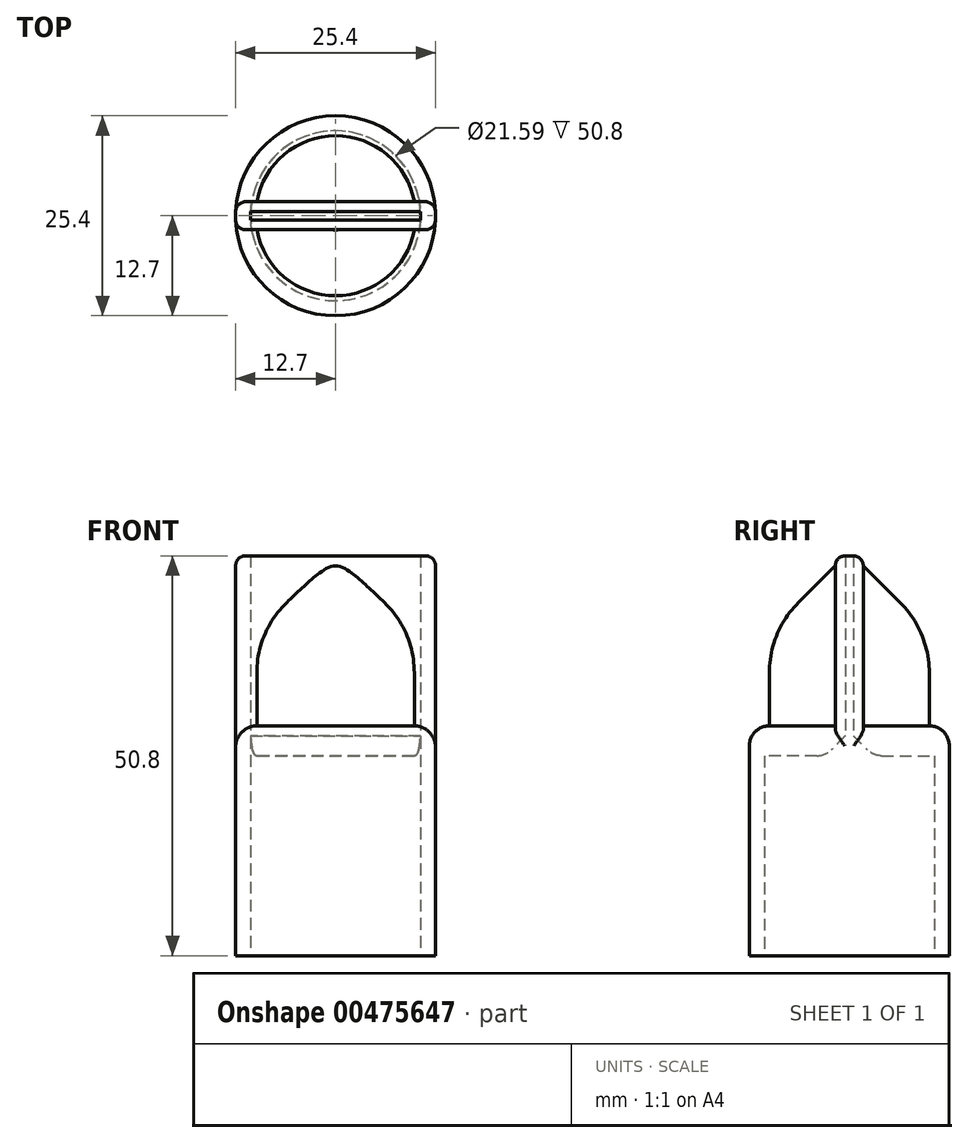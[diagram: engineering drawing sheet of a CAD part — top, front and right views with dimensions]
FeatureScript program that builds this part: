
annotation { "Feature Type Name" : "Feature", "Feature Type Description" : "" }
export const myFeature = defineFeature(function(context is Context, id is Id, definition is map)
    precondition{}
    {
        {
            var Q0;
            Q0=qCreatedBy(makeId("Top.planeOp"),FACE);
            var sketch = newSketch(context, id + "F0", { "sketchPlane" : qUnion([Q0])});
            skCircle(sketch, "E0", {"center": v(0, 0) * mm, "radius": 10.8 * mm});
            skCircle(sketch, "E1", {"center": v(0, 0) * mm, "radius": 12.7 * mm});
            skSolve(sketch);
        }
        {
            var Q0;
            Q0=makeQuery(id+"F0.imprint","IMPRINT",FACE,{"disambiguationData":[TD([[makeQuery(id+"F0.imprint","IMPRINT",EDGE,{"derivedFrom":sQuery(id+"F0.wireOp",EDGE,"E0")}),-1.0]])]});
            extrude(context, id + "F1", {"entities" : qUnion([Q0]), "depth" : 25.4 * mm});
        }
        {
            var Q0;
            Q0=makeQuery(id+"F1.opExtrude","CAP_FACE",FACE,{"disambiguationData":[OSD([sQuery(id+"F0.wireOp",EDGE,"E0"),sQuery(id+"F0.wireOp",EDGE,"E1")])],"isStart":false});
            var sketch = newSketch(context, id + "F2", { "sketchPlane" : qUnion([Q0])});
            skLineSegment(sketch, "E2", {"start": v(0, 0) * mm, "end": v(12.7, 0) * mm});
            skLineSegment(sketch, "E3", {"start": v(0, 0) * mm, "end": v(-12.7, 0) * mm});
            skLineSegment(sketch, "E4", {"start": v(0, 0) * mm, "end": v(0, -0.52) * mm});
            skLineSegment(sketch, "E5", {"start": v(0, -0.52) * mm, "end": v(12.69, -0.52) * mm});
            skLineSegment(sketch, "E6", {"start": v(0, -0.52) * mm, "end": v(-12.69, -0.52) * mm});
            skLineSegment(sketch, "E7", {"start": v(0, 0) * mm, "end": v(0, 0.5) * mm});
            skLineSegment(sketch, "E8", {"start": v(0, 0.5) * mm, "end": v(-12.7, 0.5) * mm});
            skLineSegment(sketch, "E9", {"start": v(0, 0.5) * mm, "end": v(12.69, 0.5) * mm});
            skPoint(sketch, "E9.endSnap0", {"position": v(12.69, 0.38) * mm});
            skLineSegment(sketch, "E10", {"start": v(-12.58, 1.77) * mm, "end": v(12.58, 1.77) * mm});
            skLineSegment(sketch, "E11", {"start": v(-12.57, -1.78) * mm, "end": v(12.57, -1.78) * mm});
            skSolve(sketch);
        }
        {
            var Q0;
            {var subQ0=sQuery(id+"F2.wireOp",EDGE,"E8");var subQ1=makeQuery(id+"F1.opExtrude","CAP_EDGE",EDGE,{"disambiguationData":[OSD([sQuery(id+"F0.wireOp",EDGE,"E1")])],"isStart":false});var subQ2=makeQuery(id+"F2.imprint","INTERSECT",VERTEX,{"derivedFrom":[subQ1,subQ0]});Q0=makeQuery(id+"F2.imprint","IMPRINT",FACE,{"disambiguationData":[TD([[makeQuery(id+"F2.imprint","IMPRINT",EDGE,{"disambiguationData":[TD([[subQ2,1.0]])],"derivedFrom":subQ0}),-1.0]])]});}
            var Q1;
            {var subQ0=sQuery(id+"F2.wireOp",EDGE,"E3");var subQ1=makeQuery(id+"F1.opExtrude","CAP_EDGE",EDGE,{"disambiguationData":[OSD([sQuery(id+"F0.wireOp",EDGE,"E1")])],"isStart":false});var subQ2=makeQuery(id+"F2.imprint","INTERSECT",VERTEX,{"derivedFrom":[subQ1,subQ0]});Q1=makeQuery(id+"F2.imprint","IMPRINT",FACE,{"disambiguationData":[TD([[makeQuery(id+"F2.imprint","IMPRINT",EDGE,{"disambiguationData":[TD([[subQ2,1.0]])],"derivedFrom":subQ0}),-1.0]])]});}
            var Q2;
            {var subQ0=sQuery(id+"F2.wireOp",EDGE,"E3");var subQ1=makeQuery(id+"F1.opExtrude","CAP_EDGE",EDGE,{"disambiguationData":[OSD([sQuery(id+"F0.wireOp",EDGE,"E1")])],"isStart":false});var subQ2=makeQuery(id+"F2.imprint","INTERSECT",VERTEX,{"derivedFrom":[subQ1,subQ0]});Q2=makeQuery(id+"F2.imprint","IMPRINT",FACE,{"disambiguationData":[TD([[makeQuery(id+"F2.imprint","IMPRINT",EDGE,{"disambiguationData":[TD([[subQ2,1.0]])],"derivedFrom":subQ0}),1.0]])]});}
            var Q3;
            {var subQ0=sQuery(id+"F2.wireOp",EDGE,"E6");var subQ1=makeQuery(id+"F1.opExtrude","CAP_EDGE",EDGE,{"disambiguationData":[OSD([sQuery(id+"F0.wireOp",EDGE,"E1")])],"isStart":false});var subQ2=makeQuery(id+"F2.imprint","INTERSECT",VERTEX,{"derivedFrom":[subQ1,subQ0]});Q3=makeQuery(id+"F2.imprint","IMPRINT",FACE,{"disambiguationData":[TD([[makeQuery(id+"F2.imprint","IMPRINT",EDGE,{"disambiguationData":[TD([[subQ2,1.0]])],"derivedFrom":subQ0}),1.0]])]});}
            var Q4;
            {var subQ2=sQuery(id+"F2.wireOp",EDGE,"E2");var subQ4=makeQuery(id+"F1.opExtrude","CAP_EDGE",EDGE,{"disambiguationData":[OSD([sQuery(id+"F0.wireOp",EDGE,"E1")])],"isStart":false});var subQ5=makeQuery(id+"F2.imprint","INTERSECT",VERTEX,{"derivedFrom":[subQ4,subQ2]});Q4=makeQuery(id+"F2.imprint","IMPRINT",FACE,{"disambiguationData":[TD([[makeQuery(id+"F2.imprint","IMPRINT",EDGE,{"disambiguationData":[TD([[subQ5,1.0]])],"derivedFrom":subQ2}),1.0]])]});}
            var Q5;
            {var subQ0=sQuery(id+"F2.wireOp",EDGE,"E5");var subQ1=makeQuery(id+"F1.opExtrude","CAP_EDGE",EDGE,{"disambiguationData":[OSD([sQuery(id+"F0.wireOp",EDGE,"E1")])],"isStart":false});var subQ2=makeQuery(id+"F2.imprint","INTERSECT",VERTEX,{"derivedFrom":[subQ1,subQ0]});Q5=makeQuery(id+"F2.imprint","IMPRINT",FACE,{"disambiguationData":[TD([[makeQuery(id+"F2.imprint","IMPRINT",EDGE,{"disambiguationData":[TD([[subQ2,1.0]])],"derivedFrom":subQ0}),-1.0]])]});}
            var Q6;
            {var subQ0=sQuery(id+"F2.wireOp",EDGE,"E2");var subQ1=makeQuery(id+"F1.opExtrude","CAP_EDGE",EDGE,{"disambiguationData":[OSD([sQuery(id+"F0.wireOp",EDGE,"E1")])],"isStart":false});var subQ2=makeQuery(id+"F2.imprint","INTERSECT",VERTEX,{"derivedFrom":[subQ1,subQ0]});Q6=makeQuery(id+"F2.imprint","IMPRINT",FACE,{"disambiguationData":[TD([[makeQuery(id+"F2.imprint","IMPRINT",EDGE,{"disambiguationData":[TD([[subQ2,1.0]])],"derivedFrom":subQ0}),-1.0]])]});}
            var Q7;
            {var subQ1=makeQuery(id+"F1.opExtrude","CAP_EDGE",EDGE,{"disambiguationData":[OSD([sQuery(id+"F0.wireOp",EDGE,"E0")])],"isStart":false});var subQ3=sQuery(id+"F2.wireOp",EDGE,"E10");var subQ5=makeQuery(id+"F2.imprint","INTERSECT",VERTEX,{"disambiguationData":[OD(0.0)],"derivedFrom":[subQ1,subQ3]});Q7=makeQuery(id+"F2.imprint","IMPRINT",FACE,{"disambiguationData":[TD([[makeQuery(id+"F2.imprint","IMPRINT",EDGE,{"disambiguationData":[TD([[subQ5,-1.0]])],"derivedFrom":subQ3}),-1.0]])]});}
            var Q8;
            {var subQ1=makeQuery(id+"F1.opExtrude","CAP_EDGE",EDGE,{"disambiguationData":[OSD([sQuery(id+"F0.wireOp",EDGE,"E0")])],"isStart":false});var subQ3=sQuery(id+"F2.wireOp",EDGE,"E11");var subQ5=makeQuery(id+"F2.imprint","INTERSECT",VERTEX,{"disambiguationData":[OD(0.0)],"derivedFrom":[subQ1,subQ3]});Q8=makeQuery(id+"F2.imprint","IMPRINT",FACE,{"disambiguationData":[TD([[makeQuery(id+"F2.imprint","IMPRINT",EDGE,{"disambiguationData":[TD([[subQ5,-1.0]])],"derivedFrom":subQ3}),1.0]])]});}
            extrude(context, id + "F3", {"entities" : qUnion([Q0, Q1, Q2, Q3, Q4, Q5, Q6, Q7, Q8]), "operationType" : NewBodyOperationType.ADD, "depth" : 25.4 * mm});
        }
        {
            var Q0;
            Q0=makeQuery(id+"F3.opExtrude","SWEPT_FACE",FACE,{"disambiguationData":[OSD([sQuery(id+"F2.wireOp",EDGE,"E10")])]});
            var sketch = newSketch(context, id + "F4", { "sketchPlane" : qUnion([Q0])});
            skLineSegment(sketch, "E12.bottom", {"start": v(-12.58, 25.4) * mm, "end": v(12.58, 25.4) * mm});
            skLineSegment(sketch, "E12.top", {"start": v(-12.58, 29.21) * mm, "end": v(12.58, 29.21) * mm});
            skLineSegment(sketch, "E12.left", {"start": v(-12.58, 25.4) * mm, "end": v(-12.58, 29.21) * mm});
            skLineSegment(sketch, "E12.right", {"start": v(12.58, 25.4) * mm, "end": v(12.58, 29.21) * mm});
            skSolve(sketch);
        }
        {
            var Q0;
            Q0=makeQuery(id+"F4.imprint","IMPRINT",FACE,{"disambiguationData":[TD([[makeQuery(id+"F4.imprint","IMPRINT",EDGE,{"derivedFrom":sQuery(id+"F4.wireOp",EDGE,"E12.top")}),-1.0]])]});
            extrude(context, id + "F5", {"entities" : qUnion([Q0]), "operationType" : NewBodyOperationType.ADD, "depth" : 25.4 * mm});
        }
        {
            var Q0;
            Q0=makeQuery(id+"F3.opExtrude","SWEPT_FACE",FACE,{"disambiguationData":[OSD([sQuery(id+"F2.wireOp",EDGE,"E11")])]});
            var sketch = newSketch(context, id + "F6", { "sketchPlane" : qUnion([Q0])});
            skLineSegment(sketch, "E13.bottom", {"start": v(-12.57, 25.4) * mm, "end": v(12.57, 25.4) * mm});
            skLineSegment(sketch, "E13.top", {"start": v(-12.57, 29.21) * mm, "end": v(12.57, 29.21) * mm});
            skLineSegment(sketch, "E13.left", {"start": v(-12.57, 25.4) * mm, "end": v(-12.57, 29.21) * mm});
            skLineSegment(sketch, "E13.right", {"start": v(12.57, 25.4) * mm, "end": v(12.57, 29.21) * mm});
            skSolve(sketch);
        }
        {
            var Q0;
            Q0=makeQuery(id+"F6.imprint","IMPRINT",FACE,{"disambiguationData":[TD([[makeQuery(id+"F6.imprint","IMPRINT",EDGE,{"derivedFrom":sQuery(id+"F6.wireOp",EDGE,"E13.top")}),-1.0]])]});
            extrude(context, id + "F7", {"entities" : qUnion([Q0]), "operationType" : NewBodyOperationType.ADD, "depth" : 25.4 * mm});
        }
        {
            var Q0;
            Q0=makeQuery(id+"F7.boolean.opBoolean","SPLIT",FACE,{"derivedFrom":makeQuery(id+"F7.opExtrude","SWEPT_FACE",FACE,{"disambiguationData":[OSD([sQuery(id+"F6.wireOp",EDGE,"E13.bottom")])]})});
            var Q1;
            Q1=makeQuery(id+"F5.boolean.opBoolean","SPLIT",FACE,{"derivedFrom":makeQuery(id+"F5.opExtrude","SWEPT_FACE",FACE,{"disambiguationData":[OSD([sQuery(id+"F4.wireOp",EDGE,"E12.bottom")])]})});
            extrude(context, id + "F8", {"entities" : qUnion([Q0, Q1]), "operationType" : NewBodyOperationType.REMOVE, "oppositeDirection" : true, "depth" : 25.4 * mm});
        }
        {
            var Q0;
            {var subQ0=sQuery(id+"F2.wireOp",EDGE,"E11");var subQ1=sQuery(id+"F0.wireOp",EDGE,"E1");Q0=makeQuery(id+"F7.boolean.opBoolean","SPLIT",EDGE,{"derivedFrom":makeQuery(id+"F3.opExtrude","SWEPT_EDGE",EDGE,{"disambiguationData":[OSD([subQ1,subQ0]),TDD([makeQuery(id+"F2.imprint","INTERSECT",VERTEX,{"disambiguationData":[OD(0.0)],"derivedFrom":[makeQuery(id+"F1.opExtrude","CAP_EDGE",EDGE,{"disambiguationData":[OSD([subQ1])],"isStart":false}),subQ0]})])]})});}
            var Q1;
            {var subQ0=sQuery(id+"F2.wireOp",EDGE,"E11");var subQ1=sQuery(id+"F0.wireOp",EDGE,"E1");Q1=makeQuery(id+"F7.boolean.opBoolean","SPLIT",EDGE,{"derivedFrom":makeQuery(id+"F3.opExtrude","SWEPT_EDGE",EDGE,{"disambiguationData":[OSD([subQ1,subQ0]),TDD([makeQuery(id+"F2.imprint","INTERSECT",VERTEX,{"disambiguationData":[OD(1.0)],"derivedFrom":[makeQuery(id+"F1.opExtrude","CAP_EDGE",EDGE,{"disambiguationData":[OSD([subQ1])],"isStart":false}),subQ0]})])]})});}
            var Q2;
            {var subQ0=sQuery(id+"F2.wireOp",EDGE,"E10");var subQ1=sQuery(id+"F0.wireOp",EDGE,"E1");Q2=makeQuery(id+"F5.boolean.opBoolean","SPLIT",EDGE,{"derivedFrom":makeQuery(id+"F3.opExtrude","SWEPT_EDGE",EDGE,{"disambiguationData":[OSD([subQ1,subQ0]),TDD([makeQuery(id+"F2.imprint","INTERSECT",VERTEX,{"disambiguationData":[OD(1.0)],"derivedFrom":[makeQuery(id+"F1.opExtrude","CAP_EDGE",EDGE,{"disambiguationData":[OSD([subQ1])],"isStart":false}),subQ0]})])]})});}
            var Q3;
            {var subQ0=sQuery(id+"F2.wireOp",EDGE,"E10");var subQ1=sQuery(id+"F0.wireOp",EDGE,"E1");Q3=makeQuery(id+"F5.boolean.opBoolean","SPLIT",EDGE,{"derivedFrom":makeQuery(id+"F3.opExtrude","SWEPT_EDGE",EDGE,{"disambiguationData":[OSD([subQ1,subQ0]),TDD([makeQuery(id+"F2.imprint","INTERSECT",VERTEX,{"disambiguationData":[OD(0.0)],"derivedFrom":[makeQuery(id+"F1.opExtrude","CAP_EDGE",EDGE,{"disambiguationData":[OSD([subQ1])],"isStart":false}),subQ0]})])]})});}
            fillet(context, id + "F9", {"entities" : qUnion([Q0, Q1, Q2, Q3]), "radius" : 1.27 * mm, "tangentPropagation" : true, "allowEdgeOverflow" : false});
        }
        {
            var Q0;
            {var subQ0=sQuery(id+"F0.wireOp",EDGE,"E1");var subQ1=makeQuery(id+"F1.opExtrude","CAP_EDGE",EDGE,{"disambiguationData":[OSD([subQ0])],"isStart":false});var subQ3=sQuery(id+"F2.wireOp",EDGE,"E11");Q0=makeQuery(id+"F8.boolean.opBoolean","INTERSECT",EDGE,{"derivedFrom":[makeQuery(id+"F7.opExtrude","SWEPT_FACE",FACE,{"disambiguationData":[OSD([sQuery(id+"F6.wireOp",EDGE,"E13.top")])]}),makeQuery(id+"F8.opExtrude","SWEPT_FACE",FACE,{"disambiguationData":[OSD([subQ0]),TDD([makeQuery(id+"F3.boolean.opBoolean","SPLIT",EDGE,{"disambiguationData":[TD([makeQuery(id+"F3.opExtrude","SWEPT_FACE",FACE,{"disambiguationData":[OSD([subQ3])]})])],"derivedFrom":subQ1})])]})]});}
            var Q1;
            {var subQ0=sQuery(id+"F0.wireOp",EDGE,"E1");var subQ1=makeQuery(id+"F1.opExtrude","CAP_EDGE",EDGE,{"disambiguationData":[OSD([subQ0])],"isStart":false});var subQ5=sQuery(id+"F2.wireOp",EDGE,"E10");Q1=makeQuery(id+"F8.boolean.opBoolean","INTERSECT",EDGE,{"derivedFrom":[makeQuery(id+"F5.opExtrude","SWEPT_FACE",FACE,{"disambiguationData":[OSD([sQuery(id+"F4.wireOp",EDGE,"E12.top")])]}),makeQuery(id+"F8.opExtrude","SWEPT_FACE",FACE,{"disambiguationData":[OSD([subQ0]),TDD([makeQuery(id+"F3.boolean.opBoolean","SPLIT",EDGE,{"disambiguationData":[TD([makeQuery(id+"F3.opExtrude","SWEPT_FACE",FACE,{"disambiguationData":[OSD([subQ5])]})])],"derivedFrom":subQ1})])]})]});}
            fillet(context, id + "F10", {"entities" : qUnion([Q0, Q1]), "radius" : 2.54 * mm, "tangentPropagation" : true, "allowEdgeOverflow" : false});
        }
        {
            var Q0;
            Q0=makeQuery(id+"F3.opExtrude","CAP_EDGE",EDGE,{"disambiguationData":[OSD([sQuery(id+"F2.wireOp",EDGE,"E5"),sQuery(id+"F2.wireOp",EDGE,"E6")])],"isStart":true});
            var Q1;
            Q1=makeQuery(id+"F3.opExtrude","CAP_EDGE",EDGE,{"disambiguationData":[OSD([sQuery(id+"F2.wireOp",EDGE,"E8"),sQuery(id+"F2.wireOp",EDGE,"E9")])],"isStart":true});
            chamfer(context, id + "F11", {"entities" : qUnion([Q0, Q1]), "width" : 2.54 * mm, "tangentPropagation" : true});
        }
        {
            var Q0;
            {var subQ0=sQuery(id+"FHGbkbRZZd5fJVd_1.wireOp",EDGE,"k0sFFGCa-SWWJ-xCFf-tX0p-m5kxG7faOtJC");Q0=makeQuery(id+"FhUnpWBAYJd5fCt_1.opExtrude","CAP_EDGE",EDGE,{"disambiguationData":[OSD([subQ0]),TDD([makeQuery(id+"FHGbkbRZZd5fJVd_1.imprint","IMPRINT",EDGE,{"disambiguationData":[TD([[makeQuery(id+"FHGbkbRZZd5fJVd_1.imprint","INTERSECT",VERTEX,{"disambiguationData":[OD(1.0)],"derivedFrom":[makeQuery(id+"F3.opExtrude","CAP_EDGE",EDGE,{"disambiguationData":[OSD([sQuery(id+"F2.wireOp",EDGE,"E8"),sQuery(id+"F2.wireOp",EDGE,"E9")])],"isStart":false}),subQ0]}),-1.0]])],"derivedFrom":subQ0})])],"isStart":false});}
            var Q1;
            {var subQ0=sQuery(id+"FHGbkbRZZd5fJVd_1.wireOp",EDGE,"k0sFFGCa-SWWJ-xCFf-tX0p-m5kxG7faOtJC");Q1=makeQuery(id+"FhUnpWBAYJd5fCt_1.opExtrude","CAP_EDGE",EDGE,{"disambiguationData":[OSD([subQ0]),TDD([makeQuery(id+"FHGbkbRZZd5fJVd_1.imprint","IMPRINT",EDGE,{"disambiguationData":[TD([[makeQuery(id+"FHGbkbRZZd5fJVd_1.imprint","INTERSECT",VERTEX,{"disambiguationData":[OD(0.0)],"derivedFrom":[makeQuery(id+"F3.opExtrude","CAP_EDGE",EDGE,{"disambiguationData":[OSD([sQuery(id+"F2.wireOp",EDGE,"E8"),sQuery(id+"F2.wireOp",EDGE,"E9")])],"isStart":false}),subQ0]}),1.0]])],"derivedFrom":subQ0})])],"isStart":false});}
            var Q2;
            {var subQ0=sQuery(id+"F2.wireOp",EDGE,"E9");var subQ1=sQuery(id+"F2.wireOp",EDGE,"E8");var subQ2=sQuery(id+"F2.wireOp",EDGE,"E10");var subQ3=sQuery(id+"F0.wireOp",EDGE,"E1");var subQ4=sQuery(id+"F0.wireOp",EDGE,"E0");var subQ7=sQuery(id+"F2.wireOp",EDGE,"E5");var subQ9=sQuery(id+"F2.wireOp",EDGE,"E6");Q2=makeQuery(id+"F11.opChamfer","BLEND_EDGE",EDGE,{"blendedFrom":[makeQuery(id+"F3.opExtrude","CAP_EDGE",EDGE,{"disambiguationData":[OSD([subQ1,subQ0])],"isStart":true}),makeQuery(id+"F5.boolean.opBoolean","MERGE",FACE,{"derivedFrom":[makeQuery(id+"F3.boolean.opBoolean","SPLIT",FACE,{"disambiguationData":[TD([makeQuery(id+"F3.opExtrude","SWEPT_FACE",FACE,{"disambiguationData":[OSD([subQ2])]})])],"derivedFrom":makeQuery(id+"F3.opExtrude","CAP_FACE",FACE,{"disambiguationData":[OSD([subQ4,subQ3,subQ7,subQ9,subQ1,subQ0,subQ2,sQuery(id+"F2.wireOp",EDGE,"E11")])],"isStart":true})}),makeQuery(id+"F5.opExtrude","SWEPT_FACE",FACE,{"disambiguationData":[OSD([sQuery(id+"F4.wireOp",EDGE,"E12.bottom")])]})]})],"blendedInto":[makeQuery(id+"F5.boolean.opBoolean","MERGE",FACE,{"derivedFrom":[makeQuery(id+"F3.boolean.opBoolean","SPLIT",FACE,{"disambiguationData":[TD([makeQuery(id+"F3.opExtrude","SWEPT_FACE",FACE,{"disambiguationData":[OSD([subQ2])]})])],"derivedFrom":makeQuery(id+"F3.opExtrude","CAP_FACE",FACE,{"disambiguationData":[OSD([subQ4,subQ3,subQ7,subQ9,subQ1,subQ0,subQ2,sQuery(id+"F2.wireOp",EDGE,"E11")])],"isStart":true})}),makeQuery(id+"F5.opExtrude","SWEPT_FACE",FACE,{"disambiguationData":[OSD([sQuery(id+"F4.wireOp",EDGE,"E12.bottom")])]})]})]});}
            var Q3;
            {var subQ0=sQuery(id+"F2.wireOp",EDGE,"E11");var subQ1=sQuery(id+"F2.wireOp",EDGE,"E6");var subQ2=sQuery(id+"F2.wireOp",EDGE,"E5");var subQ3=sQuery(id+"F0.wireOp",EDGE,"E1");var subQ4=sQuery(id+"F0.wireOp",EDGE,"E0");var subQ7=sQuery(id+"F2.wireOp",EDGE,"E9");var subQ9=sQuery(id+"F2.wireOp",EDGE,"E8");Q3=makeQuery(id+"F11.opChamfer","BLEND_EDGE",EDGE,{"blendedFrom":[makeQuery(id+"F3.opExtrude","CAP_EDGE",EDGE,{"disambiguationData":[OSD([subQ2,subQ1])],"isStart":true}),makeQuery(id+"F7.boolean.opBoolean","MERGE",FACE,{"derivedFrom":[makeQuery(id+"F3.boolean.opBoolean","SPLIT",FACE,{"disambiguationData":[TD([makeQuery(id+"F3.opExtrude","SWEPT_FACE",FACE,{"disambiguationData":[OSD([subQ0])]})])],"derivedFrom":makeQuery(id+"F3.opExtrude","CAP_FACE",FACE,{"disambiguationData":[OSD([subQ4,subQ3,subQ2,subQ1,subQ9,subQ7,sQuery(id+"F2.wireOp",EDGE,"E10"),subQ0])],"isStart":true})}),makeQuery(id+"F7.opExtrude","SWEPT_FACE",FACE,{"disambiguationData":[OSD([sQuery(id+"F6.wireOp",EDGE,"E13.bottom")])]})]})],"blendedInto":[makeQuery(id+"F7.boolean.opBoolean","MERGE",FACE,{"derivedFrom":[makeQuery(id+"F3.boolean.opBoolean","SPLIT",FACE,{"disambiguationData":[TD([makeQuery(id+"F3.opExtrude","SWEPT_FACE",FACE,{"disambiguationData":[OSD([subQ0])]})])],"derivedFrom":makeQuery(id+"F3.opExtrude","CAP_FACE",FACE,{"disambiguationData":[OSD([subQ4,subQ3,subQ2,subQ1,subQ9,subQ7,sQuery(id+"F2.wireOp",EDGE,"E10"),subQ0])],"isStart":true})}),makeQuery(id+"F7.opExtrude","SWEPT_FACE",FACE,{"disambiguationData":[OSD([sQuery(id+"F6.wireOp",EDGE,"E13.bottom")])]})]})]});}
            fillet(context, id + "F12", {"entities" : qUnion([Q0, Q1, Q2, Q3]), "radius" : 2.54 * mm, "tangentPropagation" : true, "allowEdgeOverflow" : false});
        }
        {
            var Q0;
            Q0=makeQuery(id+"F5.opExtrude","SWEPT_FACE",FACE,{"disambiguationData":[OSD([sQuery(id+"F4.wireOp",EDGE,"E12.top")])]});
            var Q1;
            Q1=makeQuery(id+"F7.opExtrude","SWEPT_FACE",FACE,{"disambiguationData":[OSD([sQuery(id+"F6.wireOp",EDGE,"E13.top")])]});
            extrude(context, id + "F13", {"entities" : qUnion([Q0, Q1]), "operationType" : NewBodyOperationType.ADD, "depth" : 20.32 * mm});
        }
        {
            var Q0;
            Q0=makeQuery(id+"F13.opExtrude","CAP_EDGE",EDGE,{"disambiguationData":[OSD([sQuery(id+"F0.wireOp",EDGE,"E1"),sQuery(id+"F4.wireOp",EDGE,"E12.top")])],"isStart":false});
            var Q1;
            Q1=makeQuery(id+"F13.opExtrude","CAP_EDGE",EDGE,{"disambiguationData":[OSD([sQuery(id+"F0.wireOp",EDGE,"E1"),sQuery(id+"F6.wireOp",EDGE,"E13.top")])],"isStart":false});
            chamfer(context, id + "F14", {"entities" : qUnion([Q0, Q1]), "width" : 8.36 * mm, "tangentPropagation" : true});
        }
        {
            var Q0;
            {var subQ0=sQuery(id+"F4.wireOp",EDGE,"E12.top");var subQ1=sQuery(id+"F0.wireOp",EDGE,"E1");Q0=makeQuery(id+"F14.opChamfer","BLEND_EDGE",EDGE,{"blendedFrom":[makeQuery(id+"F13.opExtrude","CAP_EDGE",EDGE,{"disambiguationData":[OSD([subQ1,subQ0])],"isStart":false}),makeQuery(id+"F13.opExtrude","SWEPT_FACE",FACE,{"disambiguationData":[OSD([subQ1,subQ0])]})],"blendedInto":[makeQuery(id+"F13.opExtrude","SWEPT_FACE",FACE,{"disambiguationData":[OSD([subQ1,subQ0])]})]});}
            var Q1;
            {var subQ0=sQuery(id+"F6.wireOp",EDGE,"E13.top");var subQ1=sQuery(id+"F0.wireOp",EDGE,"E1");Q1=makeQuery(id+"F14.opChamfer","BLEND_EDGE",EDGE,{"blendedFrom":[makeQuery(id+"F13.opExtrude","CAP_EDGE",EDGE,{"disambiguationData":[OSD([subQ1,subQ0])],"isStart":false}),makeQuery(id+"F13.opExtrude","SWEPT_FACE",FACE,{"disambiguationData":[OSD([subQ1,subQ0])]})],"blendedInto":[makeQuery(id+"F13.opExtrude","SWEPT_FACE",FACE,{"disambiguationData":[OSD([subQ1,subQ0])]})]});}
            fillet(context, id + "F15", {"entities" : qUnion([Q0, Q1]), "radius" : 12.7 * mm, "tangentPropagation" : true, "allowEdgeOverflow" : false});
        }
        {
            var Q0;
            Q0=makeQuery(id+"F3.opExtrude","CAP_EDGE",EDGE,{"disambiguationData":[OSD([sQuery(id+"F2.wireOp",EDGE,"E10")])],"isStart":false});
            var Q1;
            Q1=makeQuery(id+"F3.opExtrude","CAP_EDGE",EDGE,{"disambiguationData":[OSD([sQuery(id+"F2.wireOp",EDGE,"E11")])],"isStart":false});
            fillet(context, id + "F16", {"entities" : qUnion([Q0, Q1]), "radius" : 1.27 * mm, "tangentPropagation" : true, "allowEdgeOverflow" : false});
        }
    });
